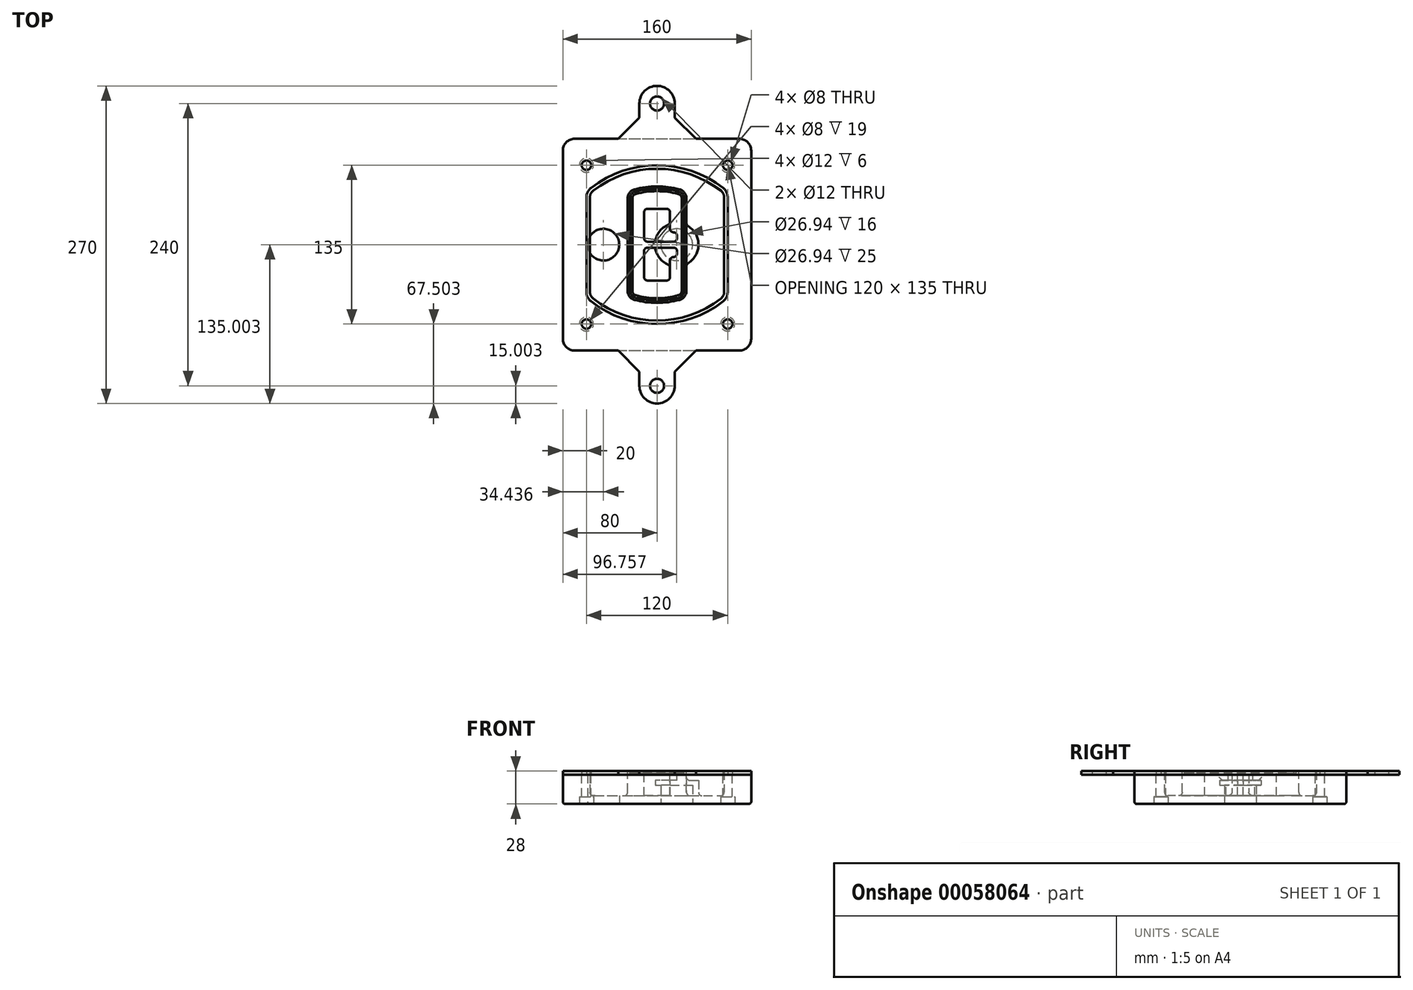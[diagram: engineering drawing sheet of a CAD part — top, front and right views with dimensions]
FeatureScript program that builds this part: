
annotation { "Feature Type Name" : "Feature", "Feature Type Description" : "" }
export const myFeature = defineFeature(function(context is Context, id is Id, definition is map)
    precondition{}
    {
        {
            var Q0;
            Q0=qCreatedBy(makeId("Top.planeOp"),FACE);
            var sketch = newSketch(context, id + "F0", { "sketchPlane" : qUnion([Q0])});
            skPoint(sketch, "E0.rect.middle", {"position": v(0, 0) * mm});
            skLineSegment(sketch, "E1.bottom", {"start": v(24.05, 28.38) * mm, "end": v(164.05, 28.38) * mm});
            skLineSegment(sketch, "E1.top", {"start": v(24.05, 208.38) * mm, "end": v(164.05, 208.38) * mm});
            skLineSegment(sketch, "E1.left", {"start": v(14.05, 38.38) * mm, "end": v(14.05, 198.38) * mm});
            skLineSegment(sketch, "E1.right", {"start": v(174.05, 38.38) * mm, "end": v(174.05, 198.38) * mm});
            skLineSegment(sketch, "E2", {"start": v(14.05, 208.38) * mm, "end": v(174.05, 28.38) * mm, "construction": true});
            skLineSegment(sketch, "E3", {"start": v(174.05, 208.38) * mm, "end": v(14.05, 28.38) * mm, "construction": true});
            skCircle(sketch, "E4", {"center": v(34.05, 185.88) * mm, "radius": 4 * mm});
            skCircle(sketch, "E5", {"center": v(154.05, 185.88) * mm, "radius": 4 * mm});
            skCircle(sketch, "E6", {"center": v(154.05, 50.88) * mm, "radius": 4 * mm});
            skCircle(sketch, "E7", {"center": v(34.05, 50.88) * mm, "radius": 4 * mm});
            skLineSegment(sketch, "E8", {"start": v(34.05, 185.88) * mm, "end": v(154.05, 185.88) * mm, "construction": true});
            skLineSegment(sketch, "E9", {"start": v(154.05, 185.88) * mm, "end": v(154.05, 50.88) * mm, "construction": true});
            skLineSegment(sketch, "E10", {"start": v(154.05, 50.88) * mm, "end": v(34.05, 50.88) * mm, "construction": true});
            skLineSegment(sketch, "E11", {"start": v(34.05, 50.88) * mm, "end": v(34.05, 185.88) * mm, "construction": true});
            skLineSegment(sketch, "E12", {"start": v(34.05, 158.68) * mm, "end": v(34.05, 78.09) * mm});
            skLineSegment(sketch, "E13", {"start": v(154.05, 158.68) * mm, "end": v(154.05, 78.09) * mm});
            skArc(sketch, "E14", {"start": v(150.2, 166.56) * mm, "mid": v(94.05, 185.88) * mm, "end": v(37.9, 166.56) * mm});
            skArc(sketch, "E15", {"start": v(37.9, 70.2) * mm, "mid": v(94.05, 50.88) * mm, "end": v(150.2, 70.2) * mm});
            skLineSegment(sketch, "E16", {"start": v(34.05, 118.38) * mm, "end": v(154.05, 118.38) * mm, "construction": true});
            skPoint(sketch, "E17.visualSharp", {"position": v(34.05, 73.38) * mm});
            skArc(sketch, "E17.filletArc", {"start": v(34.05, 78.09) * mm, "mid": v(35.06, 73.7) * mm, "end": v(37.9, 70.2) * mm});
            skPoint(sketch, "E18.visualSharp", {"position": v(34.05, 163.38) * mm});
            skArc(sketch, "E18.filletArc", {"start": v(37.9, 166.56) * mm, "mid": v(35.06, 163.06) * mm, "end": v(34.05, 158.68) * mm});
            skPoint(sketch, "E19.visualSharp", {"position": v(154.05, 163.38) * mm});
            skArc(sketch, "E19.filletArc", {"start": v(154.05, 158.68) * mm, "mid": v(153.04, 163.06) * mm, "end": v(150.2, 166.56) * mm});
            skPoint(sketch, "E20.visualSharp", {"position": v(154.05, 73.38) * mm});
            skArc(sketch, "E20.filletArc", {"start": v(150.2, 70.2) * mm, "mid": v(153.04, 73.7) * mm, "end": v(154.05, 78.09) * mm});
            skPoint(sketch, "E21.visualSharp", {"position": v(14.05, 208.38) * mm});
            skArc(sketch, "E21.filletArc", {"start": v(24.05, 208.38) * mm, "mid": v(16.98, 205.45) * mm, "end": v(14.05, 198.38) * mm});
            skPoint(sketch, "E22.visualSharp", {"position": v(174.05, 208.38) * mm});
            skArc(sketch, "E22.filletArc", {"start": v(174.05, 198.38) * mm, "mid": v(171.12, 205.45) * mm, "end": v(164.05, 208.38) * mm});
            skPoint(sketch, "E23.visualSharp", {"position": v(174.05, 28.38) * mm});
            skArc(sketch, "E23.filletArc", {"start": v(164.05, 28.38) * mm, "mid": v(171.12, 31.31) * mm, "end": v(174.05, 38.38) * mm});
            skPoint(sketch, "E24.visualSharp", {"position": v(14.05, 28.38) * mm});
            skArc(sketch, "E24.filletArc", {"start": v(14.05, 38.38) * mm, "mid": v(16.98, 31.31) * mm, "end": v(24.05, 28.38) * mm});
            skArc(sketch, "E25.0", {"start": v(151.05, 158.68) * mm, "mid": v(150.34, 161.75) * mm, "end": v(148.36, 164.2) * mm});
            skLineSegment(sketch, "E25.1", {"start": v(151.05, 158.68) * mm, "end": v(151.05, 78.09) * mm});
            skArc(sketch, "E25.2", {"start": v(148.36, 72.57) * mm, "mid": v(150.34, 75.02) * mm, "end": v(151.05, 78.09) * mm});
            skArc(sketch, "E25.3", {"start": v(39.74, 72.57) * mm, "mid": v(94.05, 53.88) * mm, "end": v(148.36, 72.57) * mm});
            skArc(sketch, "E25.4", {"start": v(37.05, 78.09) * mm, "mid": v(37.76, 75.02) * mm, "end": v(39.74, 72.57) * mm});
            skArc(sketch, "E25.5", {"start": v(148.36, 164.2) * mm, "mid": v(94.05, 182.88) * mm, "end": v(39.74, 164.2) * mm});
            skLineSegment(sketch, "E25.6", {"start": v(37.05, 158.68) * mm, "end": v(37.05, 78.09) * mm});
            skArc(sketch, "E25.7", {"start": v(39.74, 164.2) * mm, "mid": v(37.76, 161.75) * mm, "end": v(37.05, 158.68) * mm});
            skArc(sketch, "E26.0", {"start": v(35.43, 169.71) * mm, "mid": v(31.47, 164.82) * mm, "end": v(30.05, 158.68) * mm});
            skArc(sketch, "E26.1", {"start": v(152.67, 169.71) * mm, "mid": v(94.05, 189.88) * mm, "end": v(35.43, 169.71) * mm});
            skArc(sketch, "E26.2", {"start": v(158.05, 158.68) * mm, "mid": v(156.63, 164.82) * mm, "end": v(152.67, 169.71) * mm});
            skLineSegment(sketch, "E26.3", {"start": v(158.05, 158.68) * mm, "end": v(158.05, 78.09) * mm});
            skArc(sketch, "E26.4", {"start": v(152.67, 67.05) * mm, "mid": v(156.63, 71.95) * mm, "end": v(158.05, 78.09) * mm});
            skLineSegment(sketch, "E26.5", {"start": v(30.05, 158.68) * mm, "end": v(30.05, 78.09) * mm});
            skArc(sketch, "E26.6", {"start": v(35.43, 67.05) * mm, "mid": v(94.05, 46.88) * mm, "end": v(152.67, 67.05) * mm});
            skArc(sketch, "E26.7", {"start": v(30.05, 78.09) * mm, "mid": v(31.47, 71.95) * mm, "end": v(35.43, 67.05) * mm});
            skSolve(sketch);
        }
        {
            var Q0;
            Q0=makeQuery(id+"F0.imprint","IMPRINT",FACE,{"disambiguationData":[TD([[makeQuery(id+"F0.imprint","IMPRINT",EDGE,{"derivedFrom":sQuery(id+"F0.wireOp",EDGE,"E1.bottom")}),1.0]])]});
            var Q1;
            Q1=makeQuery(id+"F0.imprint","IMPRINT",FACE,{"disambiguationData":[TD([[makeQuery(id+"F0.imprint","IMPRINT",EDGE,{"derivedFrom":sQuery(id+"F0.wireOp",EDGE,"E12")}),1.0]])]});
            var Q2;
            Q2=makeQuery(id+"F0.imprint","IMPRINT",FACE,{"disambiguationData":[TD([[makeQuery(id+"F0.imprint","IMPRINT",EDGE,{"derivedFrom":sQuery(id+"F0.wireOp",EDGE,"E25.0")}),1.0]])]});
            var Q3;
            Q3=makeQuery(id+"F0.imprint","IMPRINT",FACE,{"disambiguationData":[TD([[makeQuery(id+"F0.imprint","IMPRINT",EDGE,{"derivedFrom":sQuery(id+"F0.wireOp",EDGE,"E12")}),-1.0]])]});
            extrude(context, id + "F1", {"entities" : qUnion([Q0, Q1, Q2, Q3]), "oppositeDirection" : true, "depth" : 25 * mm});
        }
        {
            var Q0;
            Q0=makeQuery(id+"F0.imprint","IMPRINT",FACE,{"disambiguationData":[TD([[makeQuery(id+"F0.imprint","IMPRINT",EDGE,{"derivedFrom":sQuery(id+"F0.wireOp",EDGE,"E12")}),1.0]])]});
            extrude(context, id + "F2", {"entities" : qUnion([Q0]), "operationType" : NewBodyOperationType.ADD, "depth" : 3 * mm});
        }
        {
            var Q0;
            Q0=makeQuery(id+"F0.imprint","IMPRINT",FACE,{"disambiguationData":[TD([[makeQuery(id+"F0.imprint","IMPRINT",EDGE,{"derivedFrom":sQuery(id+"F0.wireOp",EDGE,"E25.0")}),1.0]])]});
            extrude(context, id + "F3", {"entities" : qUnion([Q0]), "operationType" : NewBodyOperationType.REMOVE, "oppositeDirection" : true, "depth" : 18 * mm});
        }
        {
            var Q0;
            Q0=makeQuery(id+"F2.opExtrude","CAP_FACE",FACE,{"disambiguationData":[OSD([sQuery(id+"F0.wireOp",EDGE,"E12"),sQuery(id+"F0.wireOp",EDGE,"E13"),sQuery(id+"F0.wireOp",EDGE,"E14"),sQuery(id+"F0.wireOp",EDGE,"E15"),sQuery(id+"F0.wireOp",EDGE,"E17.filletArc"),sQuery(id+"F0.wireOp",EDGE,"E18.filletArc"),sQuery(id+"F0.wireOp",EDGE,"E19.filletArc"),sQuery(id+"F0.wireOp",EDGE,"E20.filletArc"),sQuery(id+"F0.wireOp",EDGE,"E25.0"),sQuery(id+"F0.wireOp",EDGE,"E25.1"),sQuery(id+"F0.wireOp",EDGE,"E25.2"),sQuery(id+"F0.wireOp",EDGE,"E25.3"),sQuery(id+"F0.wireOp",EDGE,"E25.4"),sQuery(id+"F0.wireOp",EDGE,"E25.5"),sQuery(id+"F0.wireOp",EDGE,"E25.6"),sQuery(id+"F0.wireOp",EDGE,"E25.7")])],"isStart":false});
            var sketch = newSketch(context, id + "F4", { "sketchPlane" : qUnion([Q0])});
            skArc(sketch, "E27.0", {"start": v(74.97, 71.41) * mm, "mid": v(94.05, 68.88) * mm, "end": v(113.13, 71.41) * mm});
            skArc(sketch, "E28.0", {"start": v(113.13, 165.35) * mm, "mid": v(94.05, 167.88) * mm, "end": v(74.97, 165.35) * mm});
            skLineSegment(sketch, "E29", {"start": v(69.05, 157.63) * mm, "end": v(69.05, 79.14) * mm});
            skLineSegment(sketch, "E30", {"start": v(119.05, 157.63) * mm, "end": v(119.05, 79.14) * mm});
            skLineSegment(sketch, "E31", {"start": v(69.05, 163.48) * mm, "end": v(119.05, 163.48) * mm, "construction": true});
            skLineSegment(sketch, "E32", {"start": v(69.05, 73.28) * mm, "end": v(119.05, 73.28) * mm, "construction": true});
            skPoint(sketch, "E33.visualSharp", {"position": v(69.05, 163.48) * mm});
            skArc(sketch, "E33.filletArc", {"start": v(74.97, 165.35) * mm, "mid": v(70.7, 162.5) * mm, "end": v(69.05, 157.63) * mm});
            skPoint(sketch, "E34.visualSharp", {"position": v(119.05, 163.48) * mm});
            skArc(sketch, "E34.filletArc", {"start": v(119.05, 157.63) * mm, "mid": v(117.4, 162.5) * mm, "end": v(113.13, 165.35) * mm});
            skPoint(sketch, "E35.visualSharp", {"position": v(119.05, 73.28) * mm});
            skArc(sketch, "E35.filletArc", {"start": v(113.13, 71.41) * mm, "mid": v(117.4, 74.27) * mm, "end": v(119.05, 79.14) * mm});
            skPoint(sketch, "E36.visualSharp", {"position": v(69.05, 73.28) * mm});
            skArc(sketch, "E36.filletArc", {"start": v(69.05, 79.14) * mm, "mid": v(70.7, 74.27) * mm, "end": v(74.97, 71.41) * mm});
            skArc(sketch, "E37.0", {"start": v(148.36, 164.2) * mm, "mid": v(94.05, 182.88) * mm, "end": v(39.74, 164.2) * mm});
            skArc(sketch, "E37.1", {"start": v(39.74, 164.2) * mm, "mid": v(37.76, 161.75) * mm, "end": v(37.05, 158.68) * mm});
            skLineSegment(sketch, "E37.2", {"start": v(37.05, 158.68) * mm, "end": v(37.05, 78.09) * mm});
            skArc(sketch, "E37.3", {"start": v(37.05, 78.09) * mm, "mid": v(37.76, 75.02) * mm, "end": v(39.74, 72.57) * mm});
            skArc(sketch, "E37.4", {"start": v(39.74, 72.57) * mm, "mid": v(94.05, 53.88) * mm, "end": v(148.36, 72.57) * mm});
            skArc(sketch, "E37.5", {"start": v(148.36, 72.57) * mm, "mid": v(150.34, 75.02) * mm, "end": v(151.05, 78.09) * mm});
            skLineSegment(sketch, "E37.6", {"start": v(151.05, 158.68) * mm, "end": v(151.05, 78.09) * mm});
            skArc(sketch, "E37.7", {"start": v(151.05, 158.68) * mm, "mid": v(150.34, 161.75) * mm, "end": v(148.36, 164.2) * mm});
            skLineSegment(sketch, "E38.0", {"start": v(117.05, 157.63) * mm, "end": v(117.05, 79.14) * mm});
            skArc(sketch, "E38.1", {"start": v(112.61, 73.34) * mm, "mid": v(115.81, 75.49) * mm, "end": v(117.05, 79.14) * mm});
            skArc(sketch, "E38.2", {"start": v(75.49, 73.34) * mm, "mid": v(94.05, 70.88) * mm, "end": v(112.61, 73.34) * mm});
            skArc(sketch, "E38.3", {"start": v(71.05, 79.14) * mm, "mid": v(72.29, 75.49) * mm, "end": v(75.49, 73.34) * mm});
            skLineSegment(sketch, "E38.4", {"start": v(71.05, 157.63) * mm, "end": v(71.05, 79.14) * mm});
            skArc(sketch, "E38.5", {"start": v(117.05, 157.63) * mm, "mid": v(115.81, 161.28) * mm, "end": v(112.61, 163.42) * mm});
            skArc(sketch, "E38.6", {"start": v(75.49, 163.42) * mm, "mid": v(72.29, 161.28) * mm, "end": v(71.05, 157.63) * mm});
            skArc(sketch, "E38.7", {"start": v(112.61, 163.42) * mm, "mid": v(94.05, 165.88) * mm, "end": v(75.49, 163.42) * mm});
            skArc(sketch, "E39.0", {"start": v(115.05, 157.63) * mm, "mid": v(114.23, 160.06) * mm, "end": v(112.1, 161.5) * mm});
            skLineSegment(sketch, "E39.1", {"start": v(115.05, 157.63) * mm, "end": v(115.05, 79.14) * mm});
            skArc(sketch, "E39.2", {"start": v(112.1, 75.27) * mm, "mid": v(114.23, 76.7) * mm, "end": v(115.05, 79.14) * mm});
            skArc(sketch, "E39.3", {"start": v(76, 75.27) * mm, "mid": v(94.05, 72.88) * mm, "end": v(112.1, 75.27) * mm});
            skArc(sketch, "E39.4", {"start": v(73.05, 79.14) * mm, "mid": v(73.87, 76.7) * mm, "end": v(76, 75.27) * mm});
            skArc(sketch, "E39.5", {"start": v(112.1, 161.5) * mm, "mid": v(94.05, 163.88) * mm, "end": v(76, 161.5) * mm});
            skLineSegment(sketch, "E39.6", {"start": v(73.05, 157.63) * mm, "end": v(73.05, 79.14) * mm});
            skArc(sketch, "E39.7", {"start": v(76, 161.5) * mm, "mid": v(73.87, 160.06) * mm, "end": v(73.05, 157.63) * mm});
            skLineSegment(sketch, "E40", {"start": v(69.05, 118.38) * mm, "end": v(119.05, 118.38) * mm, "construction": true});
            skLineSegment(sketch, "E41", {"start": v(83.05, 123.88) * mm, "end": v(83.05, 145.88) * mm});
            skLineSegment(sketch, "E42", {"start": v(86.05, 148.88) * mm, "end": v(102.05, 148.88) * mm});
            skLineSegment(sketch, "E43", {"start": v(105.05, 145.88) * mm, "end": v(105.05, 131.88) * mm});
            skLineSegment(sketch, "E44", {"start": v(108.05, 128.88) * mm, "end": v(108.05, 128.88) * mm});
            skLineSegment(sketch, "E45", {"start": v(111.05, 125.88) * mm, "end": v(111.05, 123.88) * mm});
            skLineSegment(sketch, "E46", {"start": v(108.05, 120.88) * mm, "end": v(86.05, 120.88) * mm});
            skPoint(sketch, "E47.visualSharp", {"position": v(83.05, 148.88) * mm});
            skArc(sketch, "E47.filletArc", {"start": v(86.05, 148.88) * mm, "mid": v(83.93, 148) * mm, "end": v(83.05, 145.88) * mm});
            skPoint(sketch, "E48.visualSharp", {"position": v(105.05, 148.88) * mm});
            skArc(sketch, "E48.filletArc", {"start": v(105.05, 145.88) * mm, "mid": v(104.17, 148) * mm, "end": v(102.05, 148.88) * mm});
            skPoint(sketch, "E49.visualSharp", {"position": v(105.05, 128.88) * mm});
            skArc(sketch, "E49.filletArc", {"start": v(105.05, 131.88) * mm, "mid": v(105.93, 129.76) * mm, "end": v(108.05, 128.88) * mm});
            skPoint(sketch, "E50.visualSharp", {"position": v(111.05, 128.88) * mm});
            skArc(sketch, "E50.filletArc", {"start": v(111.05, 125.88) * mm, "mid": v(110.17, 128) * mm, "end": v(108.05, 128.88) * mm});
            skPoint(sketch, "E51.visualSharp", {"position": v(111.05, 120.88) * mm});
            skArc(sketch, "E51.filletArc", {"start": v(108.05, 120.88) * mm, "mid": v(110.17, 121.76) * mm, "end": v(111.05, 123.88) * mm});
            skPoint(sketch, "E52.visualSharp", {"position": v(83.05, 120.88) * mm});
            skArc(sketch, "E52.filletArc", {"start": v(83.05, 123.88) * mm, "mid": v(83.93, 121.76) * mm, "end": v(86.05, 120.88) * mm});
            skLineSegment(sketch, "E53.0.MirrorCS", {"start": v(108.05, 115.88) * mm, "end": v(86.05, 115.88) * mm});
            skArc(sketch, "E54.0.MirrorCS", {"start": v(83.05, 112.88) * mm, "mid": v(83.93, 115) * mm, "end": v(86.05, 115.88) * mm});
            skLineSegment(sketch, "E55.0.MirrorCS", {"start": v(83.05, 112.88) * mm, "end": v(83.05, 90.88) * mm});
            skArc(sketch, "E56.0.MirrorCS", {"start": v(86.05, 87.88) * mm, "mid": v(83.93, 88.76) * mm, "end": v(83.05, 90.88) * mm});
            skLineSegment(sketch, "E57.0.MirrorCS", {"start": v(86.05, 87.88) * mm, "end": v(102.05, 87.88) * mm});
            skArc(sketch, "E58.0.MirrorCS", {"start": v(105.05, 90.88) * mm, "mid": v(104.17, 88.76) * mm, "end": v(102.05, 87.88) * mm});
            skLineSegment(sketch, "E59.0.MirrorCS", {"start": v(105.05, 90.88) * mm, "end": v(105.05, 104.88) * mm});
            skArc(sketch, "E60.0.MirrorCS", {"start": v(105.05, 104.88) * mm, "mid": v(105.93, 107) * mm, "end": v(108.05, 107.88) * mm});
            skArc(sketch, "E61.0.MirrorCS", {"start": v(111.05, 110.88) * mm, "mid": v(110.17, 108.76) * mm, "end": v(108.05, 107.88) * mm});
            skLineSegment(sketch, "E62.0.MirrorCS", {"start": v(111.05, 110.88) * mm, "end": v(111.05, 112.88) * mm});
            skArc(sketch, "E63.0.MirrorCS", {"start": v(108.05, 115.88) * mm, "mid": v(110.17, 115) * mm, "end": v(111.05, 112.88) * mm});
            skSolve(sketch);
        }
        {
            var Q0;
            Q0=makeQuery(id+"F4.imprint","IMPRINT",FACE,{"disambiguationData":[TD([[makeQuery(id+"F4.imprint","IMPRINT",EDGE,{"derivedFrom":sQuery(id+"F4.wireOp",EDGE,"E27.0")}),1.0]])]});
            var Q1;
            Q1=makeQuery(id+"F4.imprint","IMPRINT",FACE,{"disambiguationData":[TD([[makeQuery(id+"F4.imprint","IMPRINT",EDGE,{"derivedFrom":sQuery(id+"F4.wireOp",EDGE,"E38.0")}),-1.0]])]});
            var Q2;
            Q2=makeQuery(id+"F4.imprint","IMPRINT",FACE,{"disambiguationData":[TD([[makeQuery(id+"F4.imprint","IMPRINT",EDGE,{"derivedFrom":sQuery(id+"F4.wireOp",EDGE,"E39.0")}),1.0]])]});
            extrude(context, id + "F5", {"entities" : qUnion([Q0, Q1, Q2]), "operationType" : NewBodyOperationType.ADD, "endBound" : BoundingType.UP_TO_NEXT, "oppositeDirection" : true, "depth" : 25 * mm});
        }
        {
            var Q0;
            Q0=makeQuery(id+"F4.imprint","IMPRINT",FACE,{"disambiguationData":[TD([[makeQuery(id+"F4.imprint","IMPRINT",EDGE,{"derivedFrom":sQuery(id+"F4.wireOp",EDGE,"E38.0")}),-1.0]])]});
            extrude(context, id + "F6", {"entities" : qUnion([Q0]), "operationType" : NewBodyOperationType.REMOVE, "oppositeDirection" : true, "depth" : 2 * mm});
        }
        {
            var Q0;
            Q0=makeQuery(id+"F1.opExtrude","CAP_FACE",FACE,{"disambiguationData":[OSD([sQuery(id+"F0.wireOp",EDGE,"E1.bottom"),sQuery(id+"F0.wireOp",EDGE,"E1.top"),sQuery(id+"F0.wireOp",EDGE,"E1.left"),sQuery(id+"F0.wireOp",EDGE,"E1.right"),sQuery(id+"F0.wireOp",EDGE,"E4"),sQuery(id+"F0.wireOp",EDGE,"E5"),sQuery(id+"F0.wireOp",EDGE,"E6"),sQuery(id+"F0.wireOp",EDGE,"E7"),sQuery(id+"F0.wireOp",EDGE,"E21.filletArc"),sQuery(id+"F0.wireOp",EDGE,"E22.filletArc"),sQuery(id+"F0.wireOp",EDGE,"E23.filletArc"),sQuery(id+"F0.wireOp",EDGE,"E24.filletArc")])],"isStart":false});
            var sketch = newSketch(context, id + "F7", { "sketchPlane" : qUnion([Q0])});
            skCircle(sketch, "E64", {"center": v(110.8, -118.38) * mm, "radius": 13.47 * mm});
            skCircle(sketch, "E65", {"center": v(48.49, -118.38) * mm, "radius": 13.47 * mm});
            skLineSegment(sketch, "E66", {"start": v(174.05, -118.38) * mm, "end": v(14.05, -118.38) * mm});
            skCircle(sketch, "E67", {"center": v(110.8, -118.38) * mm, "radius": 18.47 * mm});
            skCircle(sketch, "E68", {"center": v(154.05, -185.88) * mm, "radius": 6 * mm});
            skCircle(sketch, "E69", {"center": v(34.05, -185.88) * mm, "radius": 6 * mm});
            skCircle(sketch, "E70", {"center": v(34.05, -50.88) * mm, "radius": 6 * mm});
            skCircle(sketch, "E71", {"center": v(154.05, -50.88) * mm, "radius": 6 * mm});
            skSolve(sketch);
        }
        {
            var Q0;
            {var subQ1=sQuery(id+"F7.wireOp",EDGE,"E66");var subQ4=sQuery(id+"F7.wireOp",EDGE,"E64");var subQ6=makeQuery(id+"F7.imprint","INTERSECT",VERTEX,{"disambiguationData":[OD(0.0)],"derivedFrom":[subQ4,subQ1]});Q0=makeQuery(id+"F7.imprint","IMPRINT",FACE,{"disambiguationData":[TD([[makeQuery(id+"F7.imprint","IMPRINT",EDGE,{"disambiguationData":[TD([[subQ6,-1.0]])],"derivedFrom":subQ4}),-1.0]])]});}
            var Q1;
            {var subQ0=sQuery(id+"F7.wireOp",EDGE,"E66");var subQ1=sQuery(id+"F7.wireOp",EDGE,"E64");var subQ3=makeQuery(id+"F7.imprint","INTERSECT",VERTEX,{"disambiguationData":[OD(0.0)],"derivedFrom":[subQ1,subQ0]});Q1=makeQuery(id+"F7.imprint","IMPRINT",FACE,{"disambiguationData":[TD([[makeQuery(id+"F7.imprint","IMPRINT",EDGE,{"disambiguationData":[TD([[subQ3,-1.0]])],"derivedFrom":subQ1}),1.0]])]});}
            var Q2;
            {var subQ0=sQuery(id+"F7.wireOp",EDGE,"E66");var subQ1=sQuery(id+"F7.wireOp",EDGE,"E64");var subQ3=makeQuery(id+"F7.imprint","INTERSECT",VERTEX,{"disambiguationData":[OD(0.0)],"derivedFrom":[subQ1,subQ0]});Q2=makeQuery(id+"F7.imprint","IMPRINT",FACE,{"disambiguationData":[TD([[makeQuery(id+"F7.imprint","IMPRINT",EDGE,{"disambiguationData":[TD([[subQ3,1.0]])],"derivedFrom":subQ1}),1.0]])]});}
            var Q3;
            {var subQ1=sQuery(id+"F7.wireOp",EDGE,"E66");var subQ4=sQuery(id+"F7.wireOp",EDGE,"E64");var subQ6=makeQuery(id+"F7.imprint","INTERSECT",VERTEX,{"disambiguationData":[OD(0.0)],"derivedFrom":[subQ4,subQ1]});Q3=makeQuery(id+"F7.imprint","IMPRINT",FACE,{"disambiguationData":[TD([[makeQuery(id+"F7.imprint","IMPRINT",EDGE,{"disambiguationData":[TD([[subQ6,1.0]])],"derivedFrom":subQ4}),-1.0]])]});}
            extrude(context, id + "F8", {"entities" : qUnion([Q0, Q1, Q2, Q3]), "operationType" : NewBodyOperationType.ADD, "oppositeDirection" : true, "depth" : 20 * mm});
        }
        {
            var Q0;
            {var subQ0=sQuery(id+"F7.wireOp",EDGE,"E66");var subQ1=sQuery(id+"F7.wireOp",EDGE,"E64");var subQ3=makeQuery(id+"F7.imprint","INTERSECT",VERTEX,{"disambiguationData":[OD(0.0)],"derivedFrom":[subQ1,subQ0]});Q0=makeQuery(id+"F7.imprint","IMPRINT",FACE,{"disambiguationData":[TD([[makeQuery(id+"F7.imprint","IMPRINT",EDGE,{"disambiguationData":[TD([[subQ3,-1.0]])],"derivedFrom":subQ1}),1.0]])]});}
            var Q1;
            {var subQ0=sQuery(id+"F7.wireOp",EDGE,"E66");var subQ1=sQuery(id+"F7.wireOp",EDGE,"E64");var subQ3=makeQuery(id+"F7.imprint","INTERSECT",VERTEX,{"disambiguationData":[OD(0.0)],"derivedFrom":[subQ1,subQ0]});Q1=makeQuery(id+"F7.imprint","IMPRINT",FACE,{"disambiguationData":[TD([[makeQuery(id+"F7.imprint","IMPRINT",EDGE,{"disambiguationData":[TD([[subQ3,1.0]])],"derivedFrom":subQ1}),1.0]])]});}
            extrude(context, id + "F9", {"entities" : qUnion([Q0, Q1]), "operationType" : NewBodyOperationType.REMOVE, "oppositeDirection" : true, "depth" : 16 * mm});
        }
        {
            var Q0;
            {var subQ0=sQuery(id+"F7.wireOp",EDGE,"E66");var subQ1=sQuery(id+"F7.wireOp",EDGE,"E65");var subQ3=makeQuery(id+"F7.imprint","INTERSECT",VERTEX,{"disambiguationData":[OD(0.0)],"derivedFrom":[subQ1,subQ0]});Q0=makeQuery(id+"F7.imprint","IMPRINT",FACE,{"disambiguationData":[TD([[makeQuery(id+"F7.imprint","IMPRINT",EDGE,{"disambiguationData":[TD([[subQ3,-1.0]])],"derivedFrom":subQ1}),1.0]])]});}
            var Q1;
            {var subQ0=sQuery(id+"F7.wireOp",EDGE,"E66");var subQ1=sQuery(id+"F7.wireOp",EDGE,"E65");var subQ3=makeQuery(id+"F7.imprint","INTERSECT",VERTEX,{"disambiguationData":[OD(0.0)],"derivedFrom":[subQ1,subQ0]});Q1=makeQuery(id+"F7.imprint","IMPRINT",FACE,{"disambiguationData":[TD([[makeQuery(id+"F7.imprint","IMPRINT",EDGE,{"disambiguationData":[TD([[subQ3,1.0]])],"derivedFrom":subQ1}),1.0]])]});}
            extrude(context, id + "F10", {"entities" : qUnion([Q0, Q1]), "operationType" : NewBodyOperationType.REMOVE, "oppositeDirection" : true, "depth" : 25 * mm});
        }
        {
            var Q0;
            Q0=makeQuery(id+"F7.imprint","IMPRINT",FACE,{"disambiguationData":[TD([[makeQuery(id+"F7.imprint","IMPRINT",EDGE,{"derivedFrom":sQuery(id+"F7.wireOp",EDGE,"E68")}),1.0]])]});
            var Q1;
            Q1=makeQuery(id+"F7.imprint","IMPRINT",FACE,{"disambiguationData":[TD([[makeQuery(id+"F7.imprint","IMPRINT",EDGE,{"derivedFrom":makeQuery(id+"F1.opExtrude","CAP_EDGE",EDGE,{"disambiguationData":[OSD([sQuery(id+"F0.wireOp",EDGE,"E5")])],"isStart":false})}),-1.0]])]});
            var Q2;
            Q2=makeQuery(id+"F7.imprint","IMPRINT",FACE,{"disambiguationData":[TD([[makeQuery(id+"F7.imprint","IMPRINT",EDGE,{"derivedFrom":sQuery(id+"F7.wireOp",EDGE,"E69")}),1.0]])]});
            var Q3;
            Q3=makeQuery(id+"F7.imprint","IMPRINT",FACE,{"disambiguationData":[TD([[makeQuery(id+"F7.imprint","IMPRINT",EDGE,{"derivedFrom":makeQuery(id+"F1.opExtrude","CAP_EDGE",EDGE,{"disambiguationData":[OSD([sQuery(id+"F0.wireOp",EDGE,"E4")])],"isStart":false})}),-1.0]])]});
            var Q4;
            Q4=makeQuery(id+"F7.imprint","IMPRINT",FACE,{"disambiguationData":[TD([[makeQuery(id+"F7.imprint","IMPRINT",EDGE,{"derivedFrom":sQuery(id+"F7.wireOp",EDGE,"E70")}),1.0]])]});
            var Q5;
            Q5=makeQuery(id+"F7.imprint","IMPRINT",FACE,{"disambiguationData":[TD([[makeQuery(id+"F7.imprint","IMPRINT",EDGE,{"derivedFrom":makeQuery(id+"F1.opExtrude","CAP_EDGE",EDGE,{"disambiguationData":[OSD([sQuery(id+"F0.wireOp",EDGE,"E7")])],"isStart":false})}),-1.0]])]});
            var Q6;
            Q6=makeQuery(id+"F7.imprint","IMPRINT",FACE,{"disambiguationData":[TD([[makeQuery(id+"F7.imprint","IMPRINT",EDGE,{"derivedFrom":sQuery(id+"F7.wireOp",EDGE,"E71")}),1.0]])]});
            var Q7;
            Q7=makeQuery(id+"F7.imprint","IMPRINT",FACE,{"disambiguationData":[TD([[makeQuery(id+"F7.imprint","IMPRINT",EDGE,{"derivedFrom":makeQuery(id+"F1.opExtrude","CAP_EDGE",EDGE,{"disambiguationData":[OSD([sQuery(id+"F0.wireOp",EDGE,"E6")])],"isStart":false})}),-1.0]])]});
            extrude(context, id + "F11", {"entities" : qUnion([Q0, Q1, Q2, Q3, Q4, Q5, Q6, Q7]), "operationType" : NewBodyOperationType.REMOVE, "oppositeDirection" : true, "depth" : 6 * mm});
        }
        {
            var Q0;
            Q0=makeQuery(id+"F9.boolean.opBoolean","COPY",FACE,{"derivedFrom":makeQuery(id+"F9.opExtrude","CAP_FACE",FACE,{"disambiguationData":[OSD([sQuery(id+"F7.wireOp",EDGE,"E64")])],"isStart":false})});
            var sketch = newSketch(context, id + "F12", { "sketchPlane" : qUnion([Q0])});
            skArc(sketch, "E72.0", {"start": v(105.05, -100.83) * mm, "mid": v(96.62, -106.56) * mm, "end": v(92.5, -115.88) * mm});
            skArc(sketch, "E72.1", {"start": v(92.5, -120.88) * mm, "mid": v(96.62, -130.2) * mm, "end": v(105.05, -135.93) * mm});
            skLineSegment(sketch, "E73", {"start": v(92.5, -120.88) * mm, "end": v(108.05, -120.88) * mm});
            skLineSegment(sketch, "E74.0", {"start": v(108.05, -115.88) * mm, "end": v(92.5, -115.88) * mm});
            skArc(sketch, "E74.1", {"start": v(108.05, -115.88) * mm, "mid": v(110.17, -115) * mm, "end": v(111.05, -112.88) * mm});
            skLineSegment(sketch, "E74.2", {"start": v(111.05, -110.88) * mm, "end": v(111.05, -112.88) * mm});
            skArc(sketch, "E74.3", {"start": v(111.05, -110.88) * mm, "mid": v(110.17, -108.76) * mm, "end": v(108.05, -107.88) * mm});
            skArc(sketch, "E74.4", {"start": v(105.05, -104.88) * mm, "mid": v(105.93, -107) * mm, "end": v(108.05, -107.88) * mm});
            skLineSegment(sketch, "E74.5", {"start": v(105.05, -100.83) * mm, "end": v(105.05, -104.88) * mm});
            skLineSegment(sketch, "E74.7", {"start": v(108.05, -120.88) * mm, "end": v(92.5, -120.88) * mm});
            skArc(sketch, "E74.8", {"start": v(108.05, -120.88) * mm, "mid": v(110.17, -121.76) * mm, "end": v(111.05, -123.88) * mm});
            skLineSegment(sketch, "E74.9", {"start": v(111.05, -125.88) * mm, "end": v(111.05, -123.88) * mm});
            skArc(sketch, "E74.10", {"start": v(111.05, -125.88) * mm, "mid": v(110.17, -128) * mm, "end": v(108.05, -128.88) * mm});
            skArc(sketch, "E74.11", {"start": v(105.05, -131.88) * mm, "mid": v(105.93, -129.76) * mm, "end": v(108.05, -128.88) * mm});
            skLineSegment(sketch, "E74.12", {"start": v(105.05, -135.93) * mm, "end": v(105.05, -131.88) * mm});
            skPoint(sketch, "E75.orphan", {"position": v(105.05, -145.88) * mm});
            skPoint(sketch, "E76.orphan", {"position": v(86.05, -120.88) * mm});
            skPoint(sketch, "E77.orphan", {"position": v(86.05, -115.88) * mm});
            skPoint(sketch, "E78.orphan", {"position": v(105.05, -90.88) * mm});
            skSolve(sketch);
        }
        {
            var Q0;
            {var subQ7=sQuery(id+"F12.wireOp",EDGE,"E72.0");var subQ14=sQuery(id+"F12.wireOp",EDGE,"E72.1");var subQ16=sQuery(id+"F12.wireOp",EDGE,"E74.1");var subQ18=sQuery(id+"F12.wireOp",EDGE,"E74.8");Q0=qUnion([makeQuery(id+"F12.imprint","IMPRINT",FACE,{"disambiguationData":[TD([[makeQuery(id+"F12.imprint","IMPRINT",EDGE,{"derivedFrom":subQ7}),1.0]])]}),makeQuery(id+"F12.imprint","IMPRINT",FACE,{"disambiguationData":[TD([[makeQuery(id+"F12.imprint","IMPRINT",EDGE,{"derivedFrom":subQ14}),1.0]])]}),makeQuery(id+"F12.imprint","IMPRINT",FACE,{"disambiguationData":[TD([[makeQuery(id+"F12.imprint","IMPRINT",EDGE,{"derivedFrom":subQ16}),1.0]])]}),makeQuery(id+"F12.imprint","IMPRINT",FACE,{"disambiguationData":[TD([[makeQuery(id+"F12.imprint","IMPRINT",EDGE,{"derivedFrom":subQ18}),-1.0]])]})]);}
            var Q1;
            Q1=makeQuery(id+"F5.boolean.opBoolean","SPLIT",FACE,{"disambiguationData":[TD([makeQuery(id+"F5.opExtrude","SWEPT_FACE",FACE,{"disambiguationData":[OSD([sQuery(id+"F4.wireOp",EDGE,"E41")])]})])],"derivedFrom":makeQuery(id+"F3.boolean.opBoolean","COPY",FACE,{"derivedFrom":makeQuery(id+"F3.opExtrude","CAP_FACE",FACE,{"disambiguationData":[OSD([sQuery(id+"F0.wireOp",EDGE,"E25.0"),sQuery(id+"F0.wireOp",EDGE,"E25.1"),sQuery(id+"F0.wireOp",EDGE,"E25.2"),sQuery(id+"F0.wireOp",EDGE,"E25.3"),sQuery(id+"F0.wireOp",EDGE,"E25.4"),sQuery(id+"F0.wireOp",EDGE,"E25.5"),sQuery(id+"F0.wireOp",EDGE,"E25.6"),sQuery(id+"F0.wireOp",EDGE,"E25.7")])],"isStart":false})})});
            extrude(context, id + "F13", {"entities" : qUnion([Q0]), "operationType" : NewBodyOperationType.REMOVE, "endBound" : BoundingType.UP_TO_SURFACE, "endBoundEntityFace" : qUnion([Q1]), "depth" : 25 * mm});
        }
        {
            var Q0;
            Q0=makeQuery(id+"F3.boolean.opBoolean","COPY",EDGE,{"derivedFrom":makeQuery(id+"F3.opExtrude","CAP_EDGE",EDGE,{"disambiguationData":[OSD([sQuery(id+"F0.wireOp",EDGE,"E25.6")])],"isStart":false})});
            var Q1;
            Q1=makeQuery(id+"F8.boolean.opBoolean","INTERSECT",EDGE,{"derivedFrom":[makeQuery(id+"F5.opExtrude","SWEPT_FACE",FACE,{"disambiguationData":[OSD([sQuery(id+"F4.wireOp",EDGE,"E30")])]}),makeQuery(id+"F8.opExtrude","CAP_FACE",FACE,{"disambiguationData":[OSD([sQuery(id+"F7.wireOp",EDGE,"E67")])],"isStart":false})]});
            var Q2;
            Q2=makeQuery(id+"F8.boolean.opBoolean","INTERSECT",EDGE,{"disambiguationData":[OD(1.0)],"derivedFrom":[makeQuery(id+"F5.opExtrude","SWEPT_FACE",FACE,{"disambiguationData":[OSD([sQuery(id+"F4.wireOp",EDGE,"E30")])]}),makeQuery(id+"F8.opExtrude","SWEPT_FACE",FACE,{"disambiguationData":[OSD([sQuery(id+"F7.wireOp",EDGE,"E67")])]})]});
            var Q3;
            {var subQ0=sQuery(id+"F4.wireOp",EDGE,"E30");Q3=makeQuery(id+"F8.boolean.opBoolean","SPLIT",EDGE,{"disambiguationData":[TD([makeQuery(id+"F5.opExtrude","SWEPT_FACE",FACE,{"disambiguationData":[OSD([sQuery(id+"F4.wireOp",EDGE,"E35.filletArc")])]})])],"derivedFrom":makeQuery(id+"F5.opExtrude","CAP_EDGE",EDGE,{"disambiguationData":[OSD([subQ0])],"isStart":false})});}
            var Q4;
            {var subQ0=sQuery(id+"F0.wireOp",EDGE,"E25.7");var subQ1=sQuery(id+"F0.wireOp",EDGE,"E25.1");var subQ2=sQuery(id+"F0.wireOp",EDGE,"E25.6");var subQ3=sQuery(id+"F0.wireOp",EDGE,"E25.5");var subQ4=sQuery(id+"F0.wireOp",EDGE,"E25.4");var subQ5=sQuery(id+"F0.wireOp",EDGE,"E25.0");var subQ6=sQuery(id+"F0.wireOp",EDGE,"E25.2");var subQ7=sQuery(id+"F0.wireOp",EDGE,"E25.3");Q4=makeQuery(id+"F8.boolean.opBoolean","INTERSECT",EDGE,{"derivedFrom":[makeQuery(id+"F5.boolean.opBoolean","SPLIT",FACE,{"disambiguationData":[TD([makeQuery(id+"F2.opExtrude","SWEPT_FACE",FACE,{"disambiguationData":[OSD([subQ5])]})])],"derivedFrom":makeQuery(id+"F3.boolean.opBoolean","COPY",FACE,{"derivedFrom":makeQuery(id+"F3.opExtrude","CAP_FACE",FACE,{"disambiguationData":[OSD([subQ5,subQ1,subQ6,subQ7,subQ4,subQ3,subQ2,subQ0])],"isStart":false})})}),makeQuery(id+"F8.opExtrude","SWEPT_FACE",FACE,{"disambiguationData":[OSD([sQuery(id+"F7.wireOp",EDGE,"E67")])]})]});}
            var Q5;
            Q5=makeQuery(id+"F8.boolean.opBoolean","INTERSECT",EDGE,{"disambiguationData":[OD(0.0)],"derivedFrom":[makeQuery(id+"F5.opExtrude","SWEPT_FACE",FACE,{"disambiguationData":[OSD([sQuery(id+"F4.wireOp",EDGE,"E30")])]}),makeQuery(id+"F8.opExtrude","SWEPT_FACE",FACE,{"disambiguationData":[OSD([sQuery(id+"F7.wireOp",EDGE,"E67")])]})]});
            fillet(context, id + "F14", {"entities" : qUnion([Q0, Q1, Q2, Q3, Q4, Q5]), "radius" : 3 * mm, "tangentPropagation" : true, "allowEdgeOverflow" : false});
        }
        {
            var Q0;
            Q0=makeQuery(id+"F1.opExtrude","CAP_EDGE",EDGE,{"disambiguationData":[OSD([sQuery(id+"F0.wireOp",EDGE,"E1.bottom")])],"isStart":false});
            fillet(context, id + "F15", {"entities" : qUnion([Q0]), "radius" : 2 * mm, "tangentPropagation" : true, "allowEdgeOverflow" : false});
        }
        {
            var Q0;
            {var subQ0=sQuery(id+"F0.wireOp",EDGE,"E22.filletArc");var subQ1=sQuery(id+"F0.wireOp",EDGE,"E7");var subQ2=sQuery(id+"F0.wireOp",EDGE,"E6");var subQ3=sQuery(id+"F0.wireOp",EDGE,"E5");var subQ4=sQuery(id+"F0.wireOp",EDGE,"E4");var subQ5=sQuery(id+"F0.wireOp",EDGE,"E1.bottom");var subQ6=sQuery(id+"F0.wireOp",EDGE,"E21.filletArc");var subQ7=sQuery(id+"F0.wireOp",EDGE,"E1.top");var subQ8=sQuery(id+"F0.wireOp",EDGE,"E1.left");var subQ9=sQuery(id+"F0.wireOp",EDGE,"E1.right");var subQ10=sQuery(id+"F0.wireOp",EDGE,"E23.filletArc");var subQ11=sQuery(id+"F0.wireOp",EDGE,"E24.filletArc");Q0=makeQuery(id+"F2.boolean.opBoolean","SPLIT",FACE,{"disambiguationData":[TD([makeQuery(id+"F1.opExtrude","SWEPT_FACE",FACE,{"disambiguationData":[OSD([subQ5])]})])],"derivedFrom":makeQuery(id+"F1.opExtrude","CAP_FACE",FACE,{"disambiguationData":[OSD([subQ5,subQ7,subQ8,subQ9,subQ4,subQ3,subQ2,subQ1,subQ6,subQ0,subQ10,subQ11])],"isStart":true})});}
            var sketch = newSketch(context, id + "F16", { "sketchPlane" : qUnion([Q0])});
            skLineSegment(sketch, "E79.0", {"start": v(24.05, 208.38) * mm, "end": v(164.05, 208.38) * mm});
            skArc(sketch, "E79.1", {"start": v(174.05, 198.38) * mm, "mid": v(171.12, 205.45) * mm, "end": v(164.05, 208.38) * mm});
            skLineSegment(sketch, "E79.2", {"start": v(174.05, 38.38) * mm, "end": v(174.05, 198.38) * mm});
            skArc(sketch, "E79.3", {"start": v(164.05, 28.38) * mm, "mid": v(171.12, 31.31) * mm, "end": v(174.05, 38.38) * mm});
            skLineSegment(sketch, "E79.4", {"start": v(24.05, 28.38) * mm, "end": v(164.05, 28.38) * mm});
            skArc(sketch, "E79.5", {"start": v(14.05, 38.38) * mm, "mid": v(16.98, 31.31) * mm, "end": v(24.05, 28.38) * mm});
            skLineSegment(sketch, "E79.6", {"start": v(14.05, 38.38) * mm, "end": v(14.05, 198.38) * mm});
            skArc(sketch, "E79.7", {"start": v(24.05, 208.38) * mm, "mid": v(16.98, 205.45) * mm, "end": v(14.05, 198.38) * mm});
            skCircle(sketch, "E79.8", {"center": v(34.05, 185.88) * mm, "radius": 4 * mm});
            skCircle(sketch, "E79.9", {"center": v(154.05, 185.88) * mm, "radius": 4 * mm});
            skCircle(sketch, "E79.10", {"center": v(154.05, 50.88) * mm, "radius": 4 * mm});
            skCircle(sketch, "E79.11", {"center": v(34.05, 50.88) * mm, "radius": 4 * mm});
            skArc(sketch, "E79.12", {"start": v(37.9, 70.2) * mm, "mid": v(94.05, 50.88) * mm, "end": v(150.2, 70.2) * mm});
            skArc(sketch, "E79.13", {"start": v(34.05, 78.09) * mm, "mid": v(35.06, 73.7) * mm, "end": v(37.9, 70.2) * mm});
            skLineSegment(sketch, "E79.14", {"start": v(34.05, 158.68) * mm, "end": v(34.05, 78.09) * mm});
            skArc(sketch, "E79.15", {"start": v(37.9, 166.56) * mm, "mid": v(35.06, 163.06) * mm, "end": v(34.05, 158.68) * mm});
            skArc(sketch, "E79.16", {"start": v(150.2, 166.56) * mm, "mid": v(94.05, 185.88) * mm, "end": v(37.9, 166.56) * mm});
            skArc(sketch, "E79.17", {"start": v(154.05, 158.68) * mm, "mid": v(153.04, 163.06) * mm, "end": v(150.2, 166.56) * mm});
            skLineSegment(sketch, "E79.18", {"start": v(154.05, 158.68) * mm, "end": v(154.05, 78.09) * mm});
            skArc(sketch, "E79.19", {"start": v(150.2, 70.2) * mm, "mid": v(153.04, 73.7) * mm, "end": v(154.05, 78.09) * mm});
            skLineSegment(sketch, "E80", {"start": v(61.05, 208.38) * mm, "end": v(79.05, 226.38) * mm});
            skLineSegment(sketch, "E81", {"start": v(79.05, 226.38) * mm, "end": v(79.05, 238.38) * mm});
            skCircle(sketch, "E82", {"center": v(94.05, 238.38) * mm, "radius": 6 * mm});
            skArc(sketch, "E83", {"start": v(109.05, 238.38) * mm, "mid": v(94.05, 253.38) * mm, "end": v(79.05, 238.38) * mm});
            skLineSegment(sketch, "E84", {"start": v(109.05, 238.38) * mm, "end": v(109.05, 226.38) * mm});
            skLineSegment(sketch, "E85", {"start": v(109.05, 226.38) * mm, "end": v(127.05, 208.38) * mm});
            skLineSegment(sketch, "E86", {"start": v(94.05, 238.38) * mm, "end": v(94.05, 208.38) * mm, "construction": true});
            skLineSegment(sketch, "E87", {"start": v(14.05, 118.38) * mm, "end": v(174.05, 118.38) * mm, "construction": true});
            skLineSegment(sketch, "E88.MirrorCS", {"start": v(109.05, -1.62) * mm, "end": v(109.05, 10.38) * mm});
            skLineSegment(sketch, "E89.MirrorCS", {"start": v(79.05, 10.38) * mm, "end": v(79.05, -1.62) * mm});
            skArc(sketch, "E90.MirrorCS", {"start": v(109.05, -1.62) * mm, "mid": v(94.05, -16.62) * mm, "end": v(79.05, -1.62) * mm});
            skCircle(sketch, "E91.MirrorC", {"center": v(94.05, -1.62) * mm, "radius": 6 * mm});
            skLineSegment(sketch, "E92.MirrorCS", {"start": v(109.05, 10.38) * mm, "end": v(127.05, 28.38) * mm});
            skLineSegment(sketch, "E93.MirrorCS", {"start": v(94.05, -1.62) * mm, "end": v(94.05, 28.38) * mm, "construction": true});
            skLineSegment(sketch, "E94.MirrorCS", {"start": v(61.05, 28.38) * mm, "end": v(79.05, 10.38) * mm});
            skSolve(sketch);
        }
        {
            var Q0;
            Q0 = qSketchRegion(id + "F16", true);
            var Q1;
            Q1=makeQuery(id+"F2.opExtrude","CAP_FACE",FACE,{"disambiguationData":[OSD([sQuery(id+"F0.wireOp",EDGE,"E12"),sQuery(id+"F0.wireOp",EDGE,"E13"),sQuery(id+"F0.wireOp",EDGE,"E14"),sQuery(id+"F0.wireOp",EDGE,"E15"),sQuery(id+"F0.wireOp",EDGE,"E17.filletArc"),sQuery(id+"F0.wireOp",EDGE,"E18.filletArc"),sQuery(id+"F0.wireOp",EDGE,"E19.filletArc"),sQuery(id+"F0.wireOp",EDGE,"E20.filletArc"),sQuery(id+"F0.wireOp",EDGE,"E25.0"),sQuery(id+"F0.wireOp",EDGE,"E25.1"),sQuery(id+"F0.wireOp",EDGE,"E25.2"),sQuery(id+"F0.wireOp",EDGE,"E25.3"),sQuery(id+"F0.wireOp",EDGE,"E25.4"),sQuery(id+"F0.wireOp",EDGE,"E25.5"),sQuery(id+"F0.wireOp",EDGE,"E25.6"),sQuery(id+"F0.wireOp",EDGE,"E25.7")])],"isStart":false});
            extrude(context, id + "F17", {"entities" : qUnion([Q0]), "endBound" : BoundingType.UP_TO_SURFACE, "endBoundEntityFace" : qUnion([Q1]), "depth" : 25 * mm});
        }
    });
